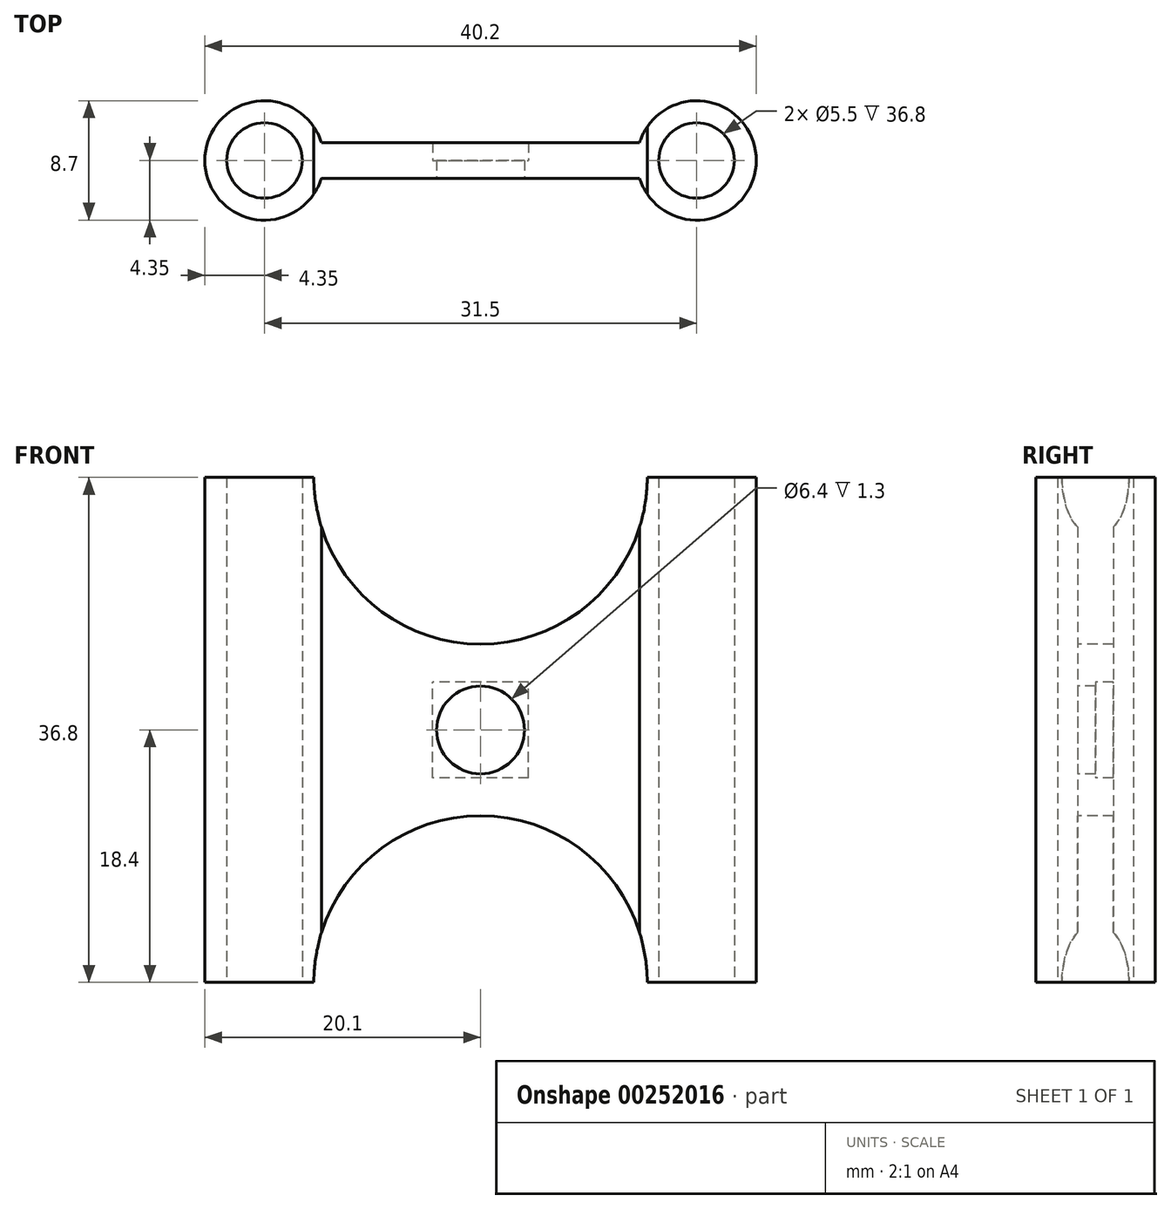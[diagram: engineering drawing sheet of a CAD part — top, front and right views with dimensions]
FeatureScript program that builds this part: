
annotation { "Feature Type Name" : "Feature", "Feature Type Description" : "" }
export const myFeature = defineFeature(function(context is Context, id is Id, definition is map)
    precondition{}
    {
        {
            var Q0;
            Q0=qCreatedBy(makeId("Top.planeOp"),FACE);
            var sketch = newSketch(context, id + "F0", { "sketchPlane" : qUnion([Q0])});
            skCircle(sketch, "E0", {"center": v(-15.75, 0) * mm, "radius": 4.35 * mm});
            skCircle(sketch, "E1", {"center": v(15.75, 0) * mm, "radius": 4.35 * mm});
            skCircle(sketch, "E2", {"center": v(-15.75, 0) * mm, "radius": 2.75 * mm});
            skCircle(sketch, "E3", {"center": v(15.75, 0) * mm, "radius": 2.75 * mm});
            skLineSegment(sketch, "E4.bottom", {"start": v(-13, 1.3) * mm, "end": v(13, 1.3) * mm});
            skLineSegment(sketch, "E4.top", {"start": v(-13, -1.3) * mm, "end": v(13, -1.3) * mm});
            skLineSegment(sketch, "E4.left", {"start": v(-13, 1.3) * mm, "end": v(-13, -1.3) * mm});
            skLineSegment(sketch, "E4.right", {"start": v(13, 1.3) * mm, "end": v(13, -1.3) * mm});
            skSolve(sketch);
        }
        {
            var Q0;
            Q0 = qSketchRegion(id + "F0", true);
            extrude(context, id + "F1", {"entities" : qUnion([Q0]), "depth" : 36.8 * mm});
        }
        {
            var Q0;
            Q0=qCreatedBy(makeId("Front.planeOp"),FACE);
            var sketch = newSketch(context, id + "F2", { "sketchPlane" : qUnion([Q0])});
            skCircle(sketch, "E5", {"center": v(0, 18.4) * mm, "radius": 3.2 * mm});
            skCircle(sketch, "E6", {"center": v(0, 0) * mm, "radius": 12.15 * mm});
            skCircle(sketch, "E7", {"center": v(0, 36.8) * mm, "radius": 12.15 * mm});
            skSolve(sketch);
        }
        {
            var Q0;
            Q0 = qSketchRegion(id + "F2", true);
            extrude(context, id + "F3", {"entities" : qUnion([Q0]), "operationType" : NewBodyOperationType.REMOVE, "endBound" : BoundingType.SYMMETRIC, "oppositeDirection" : true, "depth" : 25 * mm});
        }
        {
            var Q0;
            Q0=qCreatedBy(makeId("Front.planeOp"),FACE);
            var sketch = newSketch(context, id + "F4", { "sketchPlane" : qUnion([Q0])});
            skLineSegment(sketch, "E8.bottom", {"start": v(-3.5, 21.9) * mm, "end": v(3.5, 21.9) * mm});
            skLineSegment(sketch, "E8.top", {"start": v(-3.5, 14.9) * mm, "end": v(3.5, 14.9) * mm});
            skLineSegment(sketch, "E8.left", {"start": v(-3.5, 21.9) * mm, "end": v(-3.5, 14.9) * mm});
            skLineSegment(sketch, "E8.right", {"start": v(3.5, 21.9) * mm, "end": v(3.5, 14.9) * mm});
            skSolve(sketch);
        }
        {
            var Q0;
            Q0 = qSketchRegion(id + "F4", true);
            extrude(context, id + "F5", {"entities" : qUnion([Q0]), "operationType" : NewBodyOperationType.REMOVE, "oppositeDirection" : true, "depth" : 25 * mm});
        }
    });
